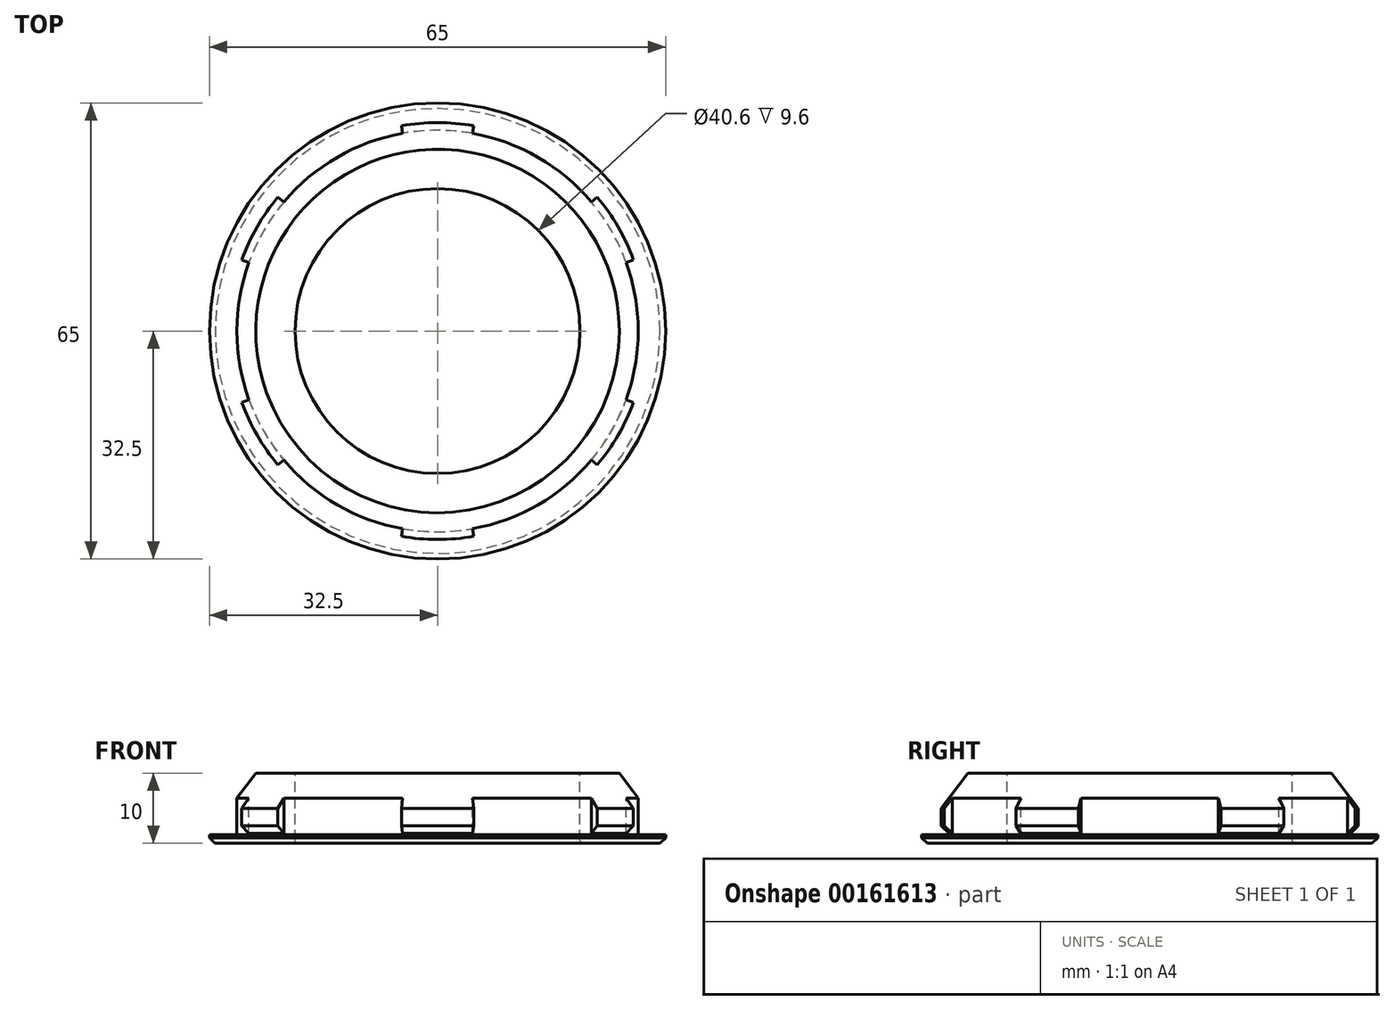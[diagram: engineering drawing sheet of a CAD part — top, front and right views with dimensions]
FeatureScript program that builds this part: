
annotation { "Feature Type Name" : "Feature", "Feature Type Description" : "" }
export const myFeature = defineFeature(function(context is Context, id is Id, definition is map)
    precondition{}
    {
        {
            var Q0;
            Q0=qCreatedBy(makeId("Front.planeOp"),FACE);
            var sketch = newSketch(context, id + "F0", { "sketchPlane" : qUnion([Q0])});
            skLineSegment(sketch, "E0", {"start": v(-32.5, 1.2) * mm, "end": v(-32.5, 0) * mm});
            skLineSegment(sketch, "E1", {"start": v(-32.5, 0) * mm, "end": v(-20.3, 0) * mm});
            skLineSegment(sketch, "E2", {"start": v(-32.5, 1.2) * mm, "end": v(-28.6, 1.2) * mm});
            skLineSegment(sketch, "E3", {"start": v(-28.6, 1.2) * mm, "end": v(-28.6, 1.4) * mm});
            skLineSegment(sketch, "E4", {"start": v(-29.7, 5) * mm, "end": v(-25.9, 10) * mm});
            skLineSegment(sketch, "E5", {"start": v(-25.9, 10) * mm, "end": v(-20.3, 10) * mm});
            skLineSegment(sketch, "E6", {"start": v(-20.3, 10) * mm, "end": v(-20.3, 0) * mm});
            skLineSegment(sketch, "E7", {"start": v(-20.3, 10) * mm, "end": v(0, 10) * mm, "construction": true});
            skLineSegment(sketch, "E8", {"start": v(0, 10) * mm, "end": v(0, 0) * mm, "construction": true});
            skLineSegment(sketch, "E9", {"start": v(0, 0) * mm, "end": v(-20.3, 0) * mm, "construction": true});
            skLineSegment(sketch, "E10", {"start": v(-29.7, 2.5) * mm, "end": v(-28.6, 1.4) * mm});
            skLineSegment(sketch, "E11", {"start": v(-29.7, 5) * mm, "end": v(-29.7, 2.5) * mm});
            skSolve(sketch);
        }
        {
            var Q0;
            Q0=qSketchRegion(id+"F0",true);
            var Q1;
            Q1=sQuery(id+"F0.wireOp",EDGE,"E8");
            revolve(context, id + "F1", {"entities" : qUnion([Q0]), "axis" : qUnion([Q1]), "revolveType" : RevolveType.FULL});
        }
        {
            var Q0;
            Q0=qCreatedBy(makeId("Front.planeOp"),FACE);
            var sketch = newSketch(context, id + "F2", { "sketchPlane" : qUnion([Q0])});
            skLineSegment(sketch, "E12", {"start": v(-28.6, 1.2) * mm, "end": v(-28.6, 10) * mm});
            skLineSegment(sketch, "E13", {"start": v(-28.6, 10) * mm, "end": v(0, 10) * mm});
            skLineSegment(sketch, "E14", {"start": v(0, 10) * mm, "end": v(0, 16) * mm});
            skLineSegment(sketch, "E15", {"start": v(0, 16) * mm, "end": v(-31, 16) * mm});
            skLineSegment(sketch, "E16", {"start": v(-31, 16) * mm, "end": v(-31, 1.2) * mm});
            skLineSegment(sketch, "E17", {"start": v(-31, 1.2) * mm, "end": v(-28.6, 1.2) * mm});
            skSolve(sketch);
        }
        {
            var Q0;
            Q0=qSketchRegion(id+"F2",true);
            var Q1;
            Q1=sQuery(id+"F2.wireOp",EDGE,"E14");
            revolve(context, id + "F3", {"entities" : qUnion([Q0]), "axis" : qUnion([Q1]), "revolveType" : RevolveType.SYMMETRIC, "angle" : 40 * degree});
        }
        {
            var Q0;
            Q0=makeQuery(id+"F3.opRevolve","SWEPT_BODY",BODY,{"disambiguationData":[OSD([sQuery(id+"F2.wireOp",EDGE,"E12"),sQuery(id+"F2.wireOp",EDGE,"E13"),sQuery(id+"F2.wireOp",EDGE,"E14"),sQuery(id+"F2.wireOp",EDGE,"E15"),sQuery(id+"F2.wireOp",EDGE,"E16"),sQuery(id+"F2.wireOp",EDGE,"E17")])]});
            var Q1;
            Q1=makeQuery(id+"F3.opRevolve","CAP_EDGE",EDGE,{"disambiguationData":[OSD([sQuery(id+"F2.wireOp",EDGE,"E14")])],"isStart":true});
            circularPattern(context, id + "F4", {"entities" : qUnion([Q0]), "axis" : qUnion([Q1]), "angle" : 360 * degree, "instanceCount" : 6, "equalSpace" : true});
        }
        {
            var Q0;
            Q0=makeQuery(id+"F4.opPattern","COPY",BODY,{"derivedFrom":makeQuery(id+"F3.opRevolve","SWEPT_BODY",BODY,{"disambiguationData":[OSD([sQuery(id+"F2.wireOp",EDGE,"E12"),sQuery(id+"F2.wireOp",EDGE,"E13"),sQuery(id+"F2.wireOp",EDGE,"E14"),sQuery(id+"F2.wireOp",EDGE,"E15"),sQuery(id+"F2.wireOp",EDGE,"E16"),sQuery(id+"F2.wireOp",EDGE,"E17")])]}),"instanceName":"7"});
            var Q1;
            Q1=makeQuery(id+"F4.opPattern","COPY",BODY,{"derivedFrom":makeQuery(id+"F3.opRevolve","SWEPT_BODY",BODY,{"disambiguationData":[OSD([sQuery(id+"F2.wireOp",EDGE,"E12"),sQuery(id+"F2.wireOp",EDGE,"E13"),sQuery(id+"F2.wireOp",EDGE,"E14"),sQuery(id+"F2.wireOp",EDGE,"E15"),sQuery(id+"F2.wireOp",EDGE,"E16"),sQuery(id+"F2.wireOp",EDGE,"E17")])]}),"instanceName":"6"});
            var Q2;
            Q2=makeQuery(id+"F4.opPattern","COPY",BODY,{"derivedFrom":makeQuery(id+"F3.opRevolve","SWEPT_BODY",BODY,{"disambiguationData":[OSD([sQuery(id+"F2.wireOp",EDGE,"E12"),sQuery(id+"F2.wireOp",EDGE,"E13"),sQuery(id+"F2.wireOp",EDGE,"E14"),sQuery(id+"F2.wireOp",EDGE,"E15"),sQuery(id+"F2.wireOp",EDGE,"E16"),sQuery(id+"F2.wireOp",EDGE,"E17")])]}),"instanceName":"5"});
            var Q3;
            Q3=makeQuery(id+"F4.opPattern","COPY",BODY,{"derivedFrom":makeQuery(id+"F3.opRevolve","SWEPT_BODY",BODY,{"disambiguationData":[OSD([sQuery(id+"F2.wireOp",EDGE,"E12"),sQuery(id+"F2.wireOp",EDGE,"E13"),sQuery(id+"F2.wireOp",EDGE,"E14"),sQuery(id+"F2.wireOp",EDGE,"E15"),sQuery(id+"F2.wireOp",EDGE,"E16"),sQuery(id+"F2.wireOp",EDGE,"E17")])]}),"instanceName":"4"});
            var Q4;
            Q4=makeQuery(id+"F4.opPattern","COPY",BODY,{"derivedFrom":makeQuery(id+"F3.opRevolve","SWEPT_BODY",BODY,{"disambiguationData":[OSD([sQuery(id+"F2.wireOp",EDGE,"E12"),sQuery(id+"F2.wireOp",EDGE,"E13"),sQuery(id+"F2.wireOp",EDGE,"E14"),sQuery(id+"F2.wireOp",EDGE,"E15"),sQuery(id+"F2.wireOp",EDGE,"E16"),sQuery(id+"F2.wireOp",EDGE,"E17")])]}),"instanceName":"3"});
            var Q5;
            Q5=makeQuery(id+"F4.opPattern","COPY",BODY,{"derivedFrom":makeQuery(id+"F3.opRevolve","SWEPT_BODY",BODY,{"disambiguationData":[OSD([sQuery(id+"F2.wireOp",EDGE,"E12"),sQuery(id+"F2.wireOp",EDGE,"E13"),sQuery(id+"F2.wireOp",EDGE,"E14"),sQuery(id+"F2.wireOp",EDGE,"E15"),sQuery(id+"F2.wireOp",EDGE,"E16"),sQuery(id+"F2.wireOp",EDGE,"E17")])]}),"instanceName":"2"});
            var Q6;
            Q6=makeQuery(id+"F4.opPattern","COPY",BODY,{"derivedFrom":makeQuery(id+"F3.opRevolve","SWEPT_BODY",BODY,{"disambiguationData":[OSD([sQuery(id+"F2.wireOp",EDGE,"E12"),sQuery(id+"F2.wireOp",EDGE,"E13"),sQuery(id+"F2.wireOp",EDGE,"E14"),sQuery(id+"F2.wireOp",EDGE,"E15"),sQuery(id+"F2.wireOp",EDGE,"E16"),sQuery(id+"F2.wireOp",EDGE,"E17")])]}),"instanceName":"1"});
            var Q7;
            Q7=makeQuery(id+"F3.opRevolve","SWEPT_BODY",BODY,{"disambiguationData":[OSD([sQuery(id+"F2.wireOp",EDGE,"E12"),sQuery(id+"F2.wireOp",EDGE,"E13"),sQuery(id+"F2.wireOp",EDGE,"E14"),sQuery(id+"F2.wireOp",EDGE,"E15"),sQuery(id+"F2.wireOp",EDGE,"E16"),sQuery(id+"F2.wireOp",EDGE,"E17")])]});
            var Q8;
            Q8=makeQuery(id+"F1.opRevolve","SWEPT_BODY",BODY,{"disambiguationData":[OSD([sQuery(id+"F0.wireOp",EDGE,"E0"),sQuery(id+"F0.wireOp",EDGE,"E1"),sQuery(id+"F0.wireOp",EDGE,"E2"),sQuery(id+"F0.wireOp",EDGE,"E3"),sQuery(id+"F0.wireOp",EDGE,"E4"),sQuery(id+"F0.wireOp",EDGE,"3N1fRAVv-PpJM-oQpf-whvB-sj1A45jDuhM4"),sQuery(id+"F0.wireOp",EDGE,"r6GXPBkd-Ub3N-YDSZ-c9t6-loZOIcQxa3wt"),sQuery(id+"F0.wireOp",EDGE,"E5"),sQuery(id+"F0.wireOp",EDGE,"E6"),sQuery(id+"F0.wireOp",EDGE,"E10"),sQuery(id+"F0.wireOp",EDGE,"E11")])]});
            booleanBodies(context, id + "F5", {"operationType" : BooleanOperationType.SUBTRACTION, "tools" : qUnion([Q0, Q1, Q2, Q3, Q4, Q5, Q6, Q7]), "targets" : qUnion([Q8])});
        }
        {
            var Q0;
            Q0=makeQuery(id+"F1.opRevolve","SWEPT_EDGE",EDGE,{"disambiguationData":[OSD([sQuery(id+"F0.wireOp",EDGE,"E1"),sQuery(id+"F0.wireOp",EDGE,"E6")])]});
            fillet(context, id + "F6", {"entities" : qUnion([Q0]), "radius" : 0.4 * mm, "tangentPropagation" : true, "allowEdgeOverflow" : false});
        }
        {
            var Q0;
            Q0=makeQuery(id+"F1.opRevolve","SWEPT_EDGE",EDGE,{"disambiguationData":[OSD([sQuery(id+"F0.wireOp",EDGE,"E0"),sQuery(id+"F0.wireOp",EDGE,"E1")])]});
            chamfer(context, id + "F7", {"entities" : qUnion([Q0]), "width" : 0.8 * mm, "tangentPropagation" : true});
        }
    });
